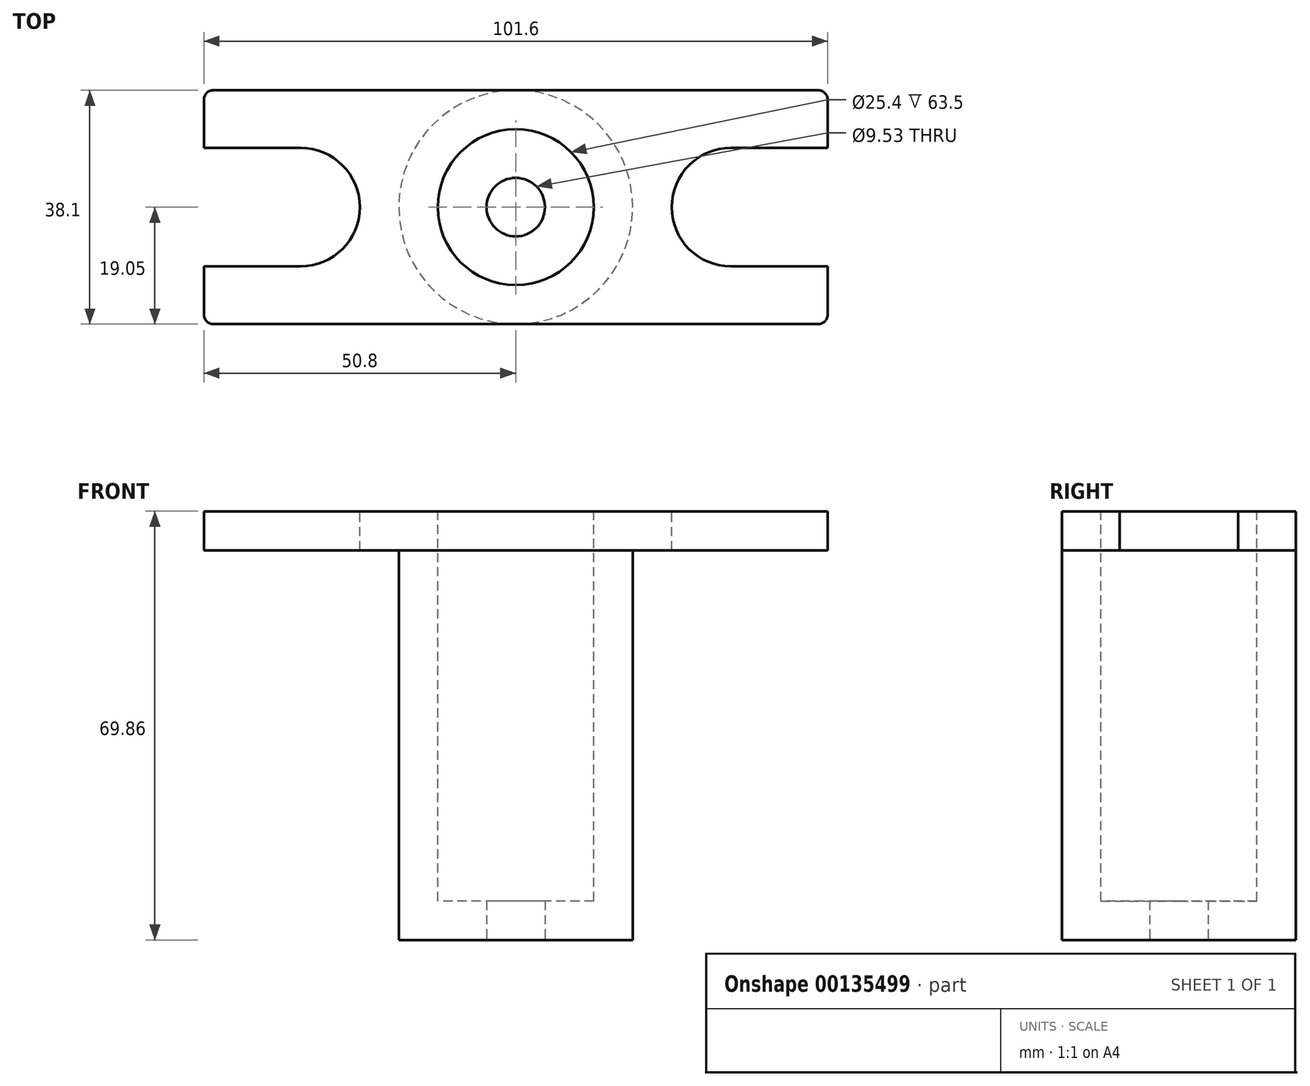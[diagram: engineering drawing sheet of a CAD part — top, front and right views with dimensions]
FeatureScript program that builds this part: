
annotation { "Feature Type Name" : "Feature", "Feature Type Description" : "" }
export const myFeature = defineFeature(function(context is Context, id is Id, definition is map)
    precondition{}
    {
        {
            var Q0;
            Q0=qCreatedBy(makeId("Top.planeOp"),FACE);
            var sketch = newSketch(context, id + "F0", { "sketchPlane" : qUnion([Q0])});
            skCircle(sketch, "E0", {"center": v(0, 0) * mm, "radius": 19.05 * mm});
            skSolve(sketch);
        }
        {
            var Q0;
            Q0=makeQuery(id+"F0.imprint","IMPRINT",FACE,{"disambiguationData":[TD([[makeQuery(id+"F0.imprint","IMPRINT",EDGE,{"derivedFrom":sQuery(id+"F0.wireOp",EDGE,"E0")}),1.0]])]});
            extrude(context, id + "F1", {"entities" : qUnion([Q0]), "endBound" : BoundingType.SYMMETRIC, "oppositeDirection" : true, "depth" : 69.85 * mm});
        }
        {
            var Q0;
            Q0=makeQuery(id+"F1.opExtrude","CAP_FACE",FACE,{"disambiguationData":[OSD([sQuery(id+"F0.wireOp",EDGE,"E0")])],"isStart":true});
            var sketch = newSketch(context, id + "F2", { "sketchPlane" : qUnion([Q0])});
            skCircle(sketch, "E1", {"center": v(0, 0) * mm, "radius": 12.7 * mm});
            skSolve(sketch);
        }
        {
            var Q0;
            Q0 = qSketchRegion(id + "F2", true);
            extrude(context, id + "F3", {"entities" : qUnion([Q0]), "operationType" : NewBodyOperationType.REMOVE, "oppositeDirection" : true, "depth" : 63.5 * mm});
        }
        {
            var Q0;
            Q0=makeQuery(id+"F1.opExtrude","CAP_FACE",FACE,{"disambiguationData":[OSD([sQuery(id+"F0.wireOp",EDGE,"E0")])],"isStart":false});
            var sketch = newSketch(context, id + "F4", { "sketchPlane" : qUnion([Q0])});
            skCircle(sketch, "E2", {"center": v(0, 0) * mm, "radius": 4.76 * mm});
            skSolve(sketch);
        }
        {
            var Q0;
            Q0 = qSketchRegion(id + "F4", true);
            extrude(context, id + "F5", {"entities" : qUnion([Q0]), "operationType" : NewBodyOperationType.REMOVE, "endBound" : BoundingType.THROUGH_ALL, "oppositeDirection" : true, "depth" : 25.4 * mm});
        }
        {
            var Q0;
            Q0=makeQuery(id+"F1.opExtrude","CAP_FACE",FACE,{"disambiguationData":[OSD([sQuery(id+"F0.wireOp",EDGE,"E0")])],"isStart":true});
            var sketch = newSketch(context, id + "F6", { "sketchPlane" : qUnion([Q0])});
            skLineSegment(sketch, "E3.bottom", {"start": v(-49.28, 19.05) * mm, "end": v(49.28, 19.05) * mm});
            skLineSegment(sketch, "E3.top", {"start": v(-49.28, -19.05) * mm, "end": v(49.28, -19.05) * mm});
            skPoint(sketch, "E4.visualSharp", {"position": v(-49.28, 19.05) * mm});
            skArc(sketch, "E4.filletArc", {"start": v(-49.28, 19.05) * mm, "mid": v(-50.35, 18.6) * mm, "end": v(-50.8, 17.53) * mm});
            skPoint(sketch, "E5.visualSharp", {"position": v(-49.28, -19.05) * mm});
            skArc(sketch, "E5.filletArc", {"start": v(-50.8, -17.53) * mm, "mid": v(-50.35, -18.6) * mm, "end": v(-49.28, -19.05) * mm});
            skPoint(sketch, "E6.visualSharp", {"position": v(49.28, 19.05) * mm});
            skArc(sketch, "E6.filletArc", {"start": v(50.8, 17.53) * mm, "mid": v(50.35, 18.6) * mm, "end": v(49.28, 19.05) * mm});
            skPoint(sketch, "E7.visualSharp", {"position": v(49.28, -19.05) * mm});
            skArc(sketch, "E7.filletArc", {"start": v(49.28, -19.05) * mm, "mid": v(50.35, -18.6) * mm, "end": v(50.8, -17.53) * mm});
            skLineSegment(sketch, "E8", {"start": v(-50.8, 17.53) * mm, "end": v(-50.8, 9.65) * mm});
            skLineSegment(sketch, "E9", {"start": v(-50.8, 9.65) * mm, "end": v(-35.05, 9.65) * mm});
            skArc(sketch, "E10", {"start": v(-35.05, -9.65) * mm, "mid": v(-25.4, 0) * mm, "end": v(-35.05, 9.65) * mm});
            skLineSegment(sketch, "E11", {"start": v(-35.05, -9.65) * mm, "end": v(-50.8, -9.65) * mm});
            skLineSegment(sketch, "E12", {"start": v(-50.8, -9.65) * mm, "end": v(-50.8, -17.53) * mm});
            skLineSegment(sketch, "E13", {"start": v(50.8, 17.53) * mm, "end": v(50.8, 9.65) * mm});
            skLineSegment(sketch, "E14", {"start": v(50.8, 9.65) * mm, "end": v(35.05, 9.65) * mm});
            skArc(sketch, "E15", {"start": v(35.05, 9.65) * mm, "mid": v(25.4, 0) * mm, "end": v(35.05, -9.65) * mm});
            skLineSegment(sketch, "E16", {"start": v(35.05, -9.65) * mm, "end": v(50.8, -9.65) * mm});
            skLineSegment(sketch, "E17", {"start": v(50.8, -9.65) * mm, "end": v(50.8, -17.53) * mm});
            skSolve(sketch);
        }
        {
            var Q0;
            {var subQ1=sQuery(id+"F6.wireOp",EDGE,"E4.filletArc");Q0=makeQuery(id+"F6.imprint","IMPRINT",FACE,{"disambiguationData":[TD([[makeQuery(id+"F6.imprint","IMPRINT",EDGE,{"derivedFrom":subQ1}),1.0]])]});}
            var Q1;
            {var subQ0=sQuery(id+"F6.wireOp",EDGE,"E6.filletArc");Q1=makeQuery(id+"F6.imprint","IMPRINT",FACE,{"disambiguationData":[TD([[makeQuery(id+"F6.imprint","IMPRINT",EDGE,{"derivedFrom":subQ0}),1.0]])]});}
            extrude(context, id + "F7", {"entities" : qUnion([Q0, Q1]), "operationType" : NewBodyOperationType.ADD, "oppositeDirection" : true, "depth" : 6.35 * mm});
        }
    });
